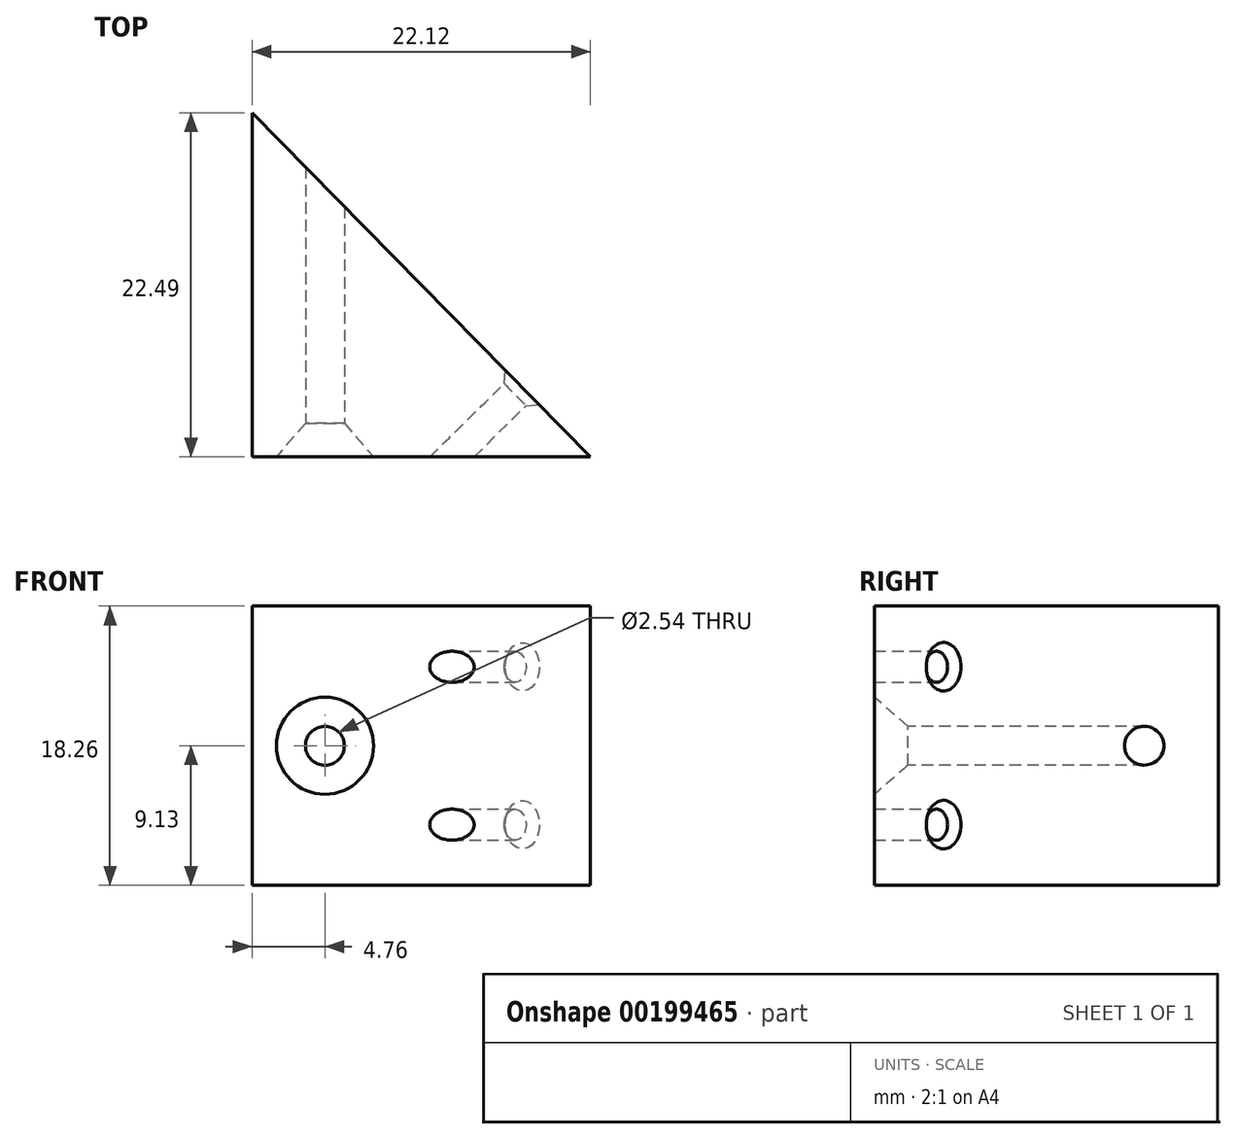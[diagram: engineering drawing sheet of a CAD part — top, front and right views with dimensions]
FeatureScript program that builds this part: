
annotation { "Feature Type Name" : "Feature", "Feature Type Description" : "" }
export const myFeature = defineFeature(function(context is Context, id is Id, definition is map)
    precondition{}
    {
        {
            var Q0;
            Q0=qCreatedBy(makeId("Top.planeOp"),FACE);
            var sketch = newSketch(context, id + "F0", { "sketchPlane" : qUnion([Q0])});
            skLineSegment(sketch, "E0", {"start": v(6.27, -22.78) * mm, "end": v(22.68, -6.64) * mm, "construction": true});
            skLineSegment(sketch, "E1", {"start": v(22.68, -6.64) * mm, "end": v(-21.85, 38.63) * mm, "construction": true});
            skLineSegment(sketch, "E2", {"start": v(-21.85, 38.63) * mm, "end": v(-38.26, 22.49) * mm, "construction": true});
            skLineSegment(sketch, "E3", {"start": v(-38.26, 22.49) * mm, "end": v(6.27, -22.78) * mm, "construction": true});
            skLineSegment(sketch, "E4", {"start": v(-38.26, 22.49) * mm, "end": v(-38.26, 0) * mm});
            skLineSegment(sketch, "E5", {"start": v(-38.26, 0) * mm, "end": v(-16.14, 0) * mm});
            skLineSegment(sketch, "E6", {"start": v(-38.26, 22.49) * mm, "end": v(-16.14, 0) * mm});
            skSolve(sketch);
        }
        {
            var Q0;
            Q0 = qSketchRegion(id + "F0", true);
            extrude(context, id + "F1", {"entities" : qUnion([Q0]), "endBound" : BoundingType.SYMMETRIC, "depth" : 18.26 * mm});
        }
        {
            var Q0;
            Q0=makeQuery(id+"F1.opExtrude","SWEPT_FACE",FACE,{"disambiguationData":[OSD([sQuery(id+"F0.wireOp",EDGE,"E6")])]});
            var sketch = newSketch(context, id + "F2", { "sketchPlane" : qUnion([Q0])});
            skPoint(sketch, "E7", {"position": v(17.67, 5.16) * mm});
            skPoint(sketch, "E8", {"position": v(17.67, -5.16) * mm});
            skSolve(sketch);
        }
        {
            var Q0;
            Q0=sQuery(id+"F2.wireOp",VERTEX,"E8");
            var Q1;
            Q1=sQuery(id+"F2.wireOp",VERTEX,"E7");
            var Q2;
            Q2=makeQuery(id+"F1.opExtrude","SWEPT_BODY",BODY,{"disambiguationData":[OSD([sQuery(id+"F0.wireOp",EDGE,"E4"),sQuery(id+"F0.wireOp",EDGE,"E5"),sQuery(id+"F0.wireOp",EDGE,"E6")])]});
            hole(context, id + "F3", {"style" : HoleStyle.C_SINK, "endStyle" : HoleEndStyle.THROUGH, "holeDiameter" : 2.03 * mm, "cSinkDiameter" : 3.17 * mm, "cSinkAngle" : 82 * degree, "startFromSketch" : true, "locations" : qUnion([Q0, Q1]), "scope" : qUnion([Q2]), "isTappedThrough" : true});
        }
        {
            var Q0;
            Q0=makeQuery(id+"F1.opExtrude","SWEPT_FACE",FACE,{"disambiguationData":[OSD([sQuery(id+"F0.wireOp",EDGE,"E5")])]});
            var sketch = newSketch(context, id + "F4", { "sketchPlane" : qUnion([Q0])});
            skPoint(sketch, "E9", {"position": v(-33.5, 0) * mm});
            skPoint(sketch, "E9.positionSnap0", {"position": v(-38.26, 0) * mm});
            skSolve(sketch);
        }
        {
            var Q0;
            Q0=sQuery(id+"F4.wireOp",VERTEX,"E9");
            var Q1;
            Q1=makeQuery(id+"F1.opExtrude","SWEPT_BODY",BODY,{"disambiguationData":[OSD([sQuery(id+"F0.wireOp",EDGE,"E4"),sQuery(id+"F0.wireOp",EDGE,"E5"),sQuery(id+"F0.wireOp",EDGE,"E6")])]});
            hole(context, id + "F5", {"style" : HoleStyle.C_SINK, "endStyle" : HoleEndStyle.THROUGH, "holeDiameter" : 2.54 * mm, "cSinkDiameter" : 6.35 * mm, "cSinkAngle" : 82 * degree, "startFromSketch" : true, "locations" : qUnion([Q0]), "scope" : qUnion([Q1]), "isTappedThrough" : true});
        }
    });
